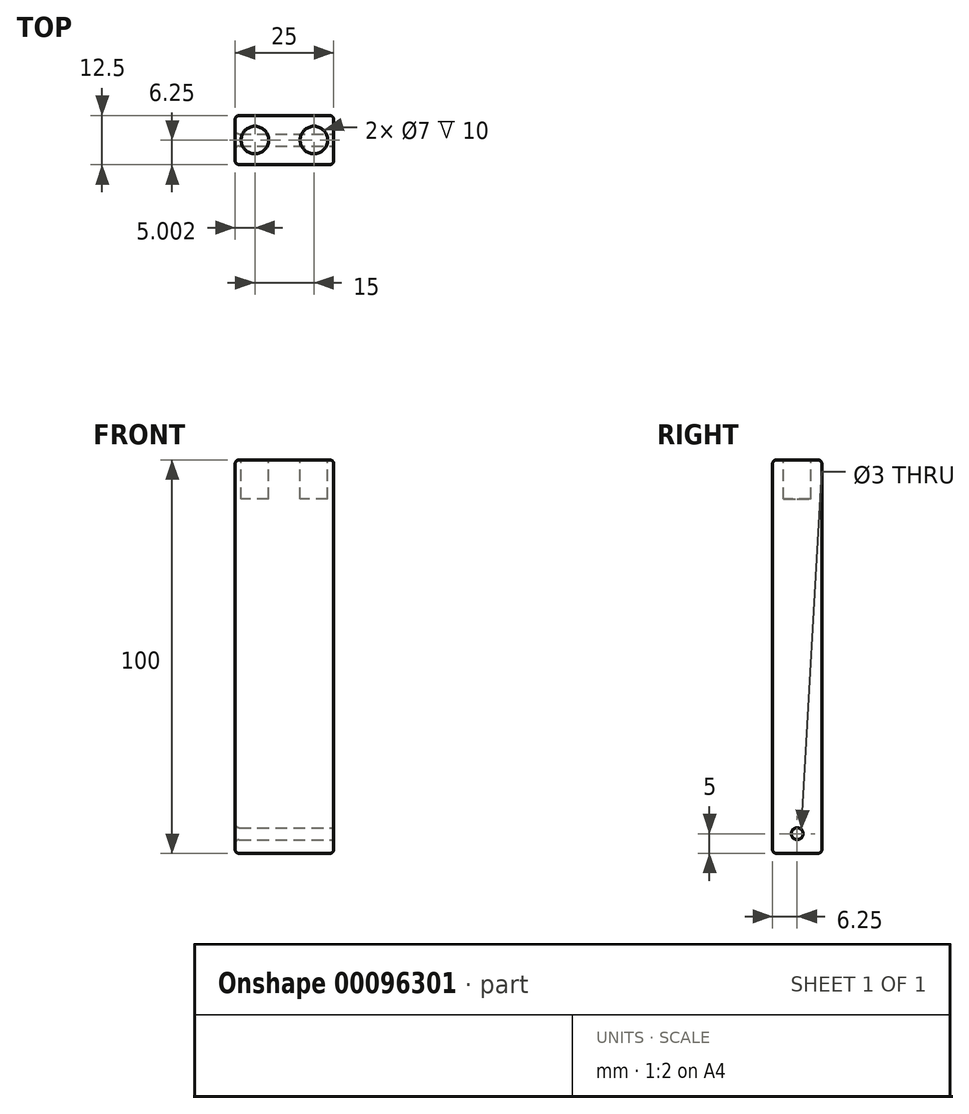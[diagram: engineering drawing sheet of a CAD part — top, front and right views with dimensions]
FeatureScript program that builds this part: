
annotation { "Feature Type Name" : "Feature", "Feature Type Description" : "" }
export const myFeature = defineFeature(function(context is Context, id is Id, definition is map)
    precondition{}
    {
        {
            var Q0;
            Q0=qCreatedBy(makeId("Front.planeOp"),FACE);
            var sketch = newSketch(context, id + "F0", { "sketchPlane" : qUnion([Q0])});
            skLineSegment(sketch, "E0.bottom", {"start": v(-26.19, 55.24) * mm, "end": v(-1.19, 55.24) * mm});
            skLineSegment(sketch, "E0.top", {"start": v(-26.19, -44.76) * mm, "end": v(-1.19, -44.76) * mm});
            skLineSegment(sketch, "E0.left", {"start": v(-26.19, 55.24) * mm, "end": v(-26.19, -44.76) * mm});
            skLineSegment(sketch, "E0.right", {"start": v(-1.19, 55.24) * mm, "end": v(-1.19, -44.76) * mm});
            skSolve(sketch);
        }
        {
            var Q0;
            Q0 = qSketchRegion(id + "F0", true);
            extrude(context, id + "F1", {"entities" : qUnion([Q0]), "depth" : 12.5 * mm});
        }
        {
            var Q0;
            Q0=qCreatedBy(makeId("Right.planeOp"),FACE);
            var sketch = newSketch(context, id + "F2", { "sketchPlane" : qUnion([Q0])});
            skCircle(sketch, "E1", {"center": v(-6.25, -39.76) * mm, "radius": 1.5 * mm});
            skSolve(sketch);
        }
        {
            var Q0;
            Q0 = qSketchRegion(id + "F2", true);
            extrude(context, id + "F3", {"entities" : qUnion([Q0]), "operationType" : NewBodyOperationType.REMOVE, "oppositeDirection" : true, "depth" : 27.2 * mm});
        }
        {
            var Q0;
            Q0=makeQuery(id+"F1.opExtrude","SWEPT_FACE",FACE,{"disambiguationData":[OSD([sQuery(id+"F0.wireOp",EDGE,"E0.bottom")])]});
            var sketch = newSketch(context, id + "F4", { "sketchPlane" : qUnion([Q0])});
            skCircle(sketch, "E2", {"center": v(-6.19, -6.25) * mm, "radius": 3.5 * mm});
            skCircle(sketch, "E3", {"center": v(-21.19, -6.25) * mm, "radius": 3.5 * mm});
            skSolve(sketch);
        }
        {
            var Q0;
            Q0 = qSketchRegion(id + "F4", true);
            extrude(context, id + "F5", {"entities" : qUnion([Q0]), "operationType" : NewBodyOperationType.REMOVE, "oppositeDirection" : true, "depth" : 10 * mm});
        }
        {
            var Q0;
            Q0=makeQuery(id+"F1.opExtrude","SWEPT_EDGE",EDGE,{"disambiguationData":[OSD([sQuery(id+"F0.wireOp",EDGE,"E0.bottom"),sQuery(id+"F0.wireOp",EDGE,"E0.left")])]});
            var Q1;
            Q1=makeQuery(id+"F1.opExtrude","CAP_EDGE",EDGE,{"disambiguationData":[OSD([sQuery(id+"F0.wireOp",EDGE,"E0.bottom")])],"isStart":false});
            var Q2;
            Q2=makeQuery(id+"F1.opExtrude","SWEPT_EDGE",EDGE,{"disambiguationData":[OSD([sQuery(id+"F0.wireOp",EDGE,"E0.bottom"),sQuery(id+"F0.wireOp",EDGE,"E0.right")])]});
            var Q3;
            Q3=makeQuery(id+"F1.opExtrude","CAP_EDGE",EDGE,{"disambiguationData":[OSD([sQuery(id+"F0.wireOp",EDGE,"E0.bottom")])],"isStart":true});
            var Q4;
            Q4=makeQuery(id+"F1.opExtrude","CAP_EDGE",EDGE,{"disambiguationData":[OSD([sQuery(id+"F0.wireOp",EDGE,"E0.left")])],"isStart":true});
            var Q5;
            Q5=makeQuery(id+"F1.opExtrude","CAP_EDGE",EDGE,{"disambiguationData":[OSD([sQuery(id+"F0.wireOp",EDGE,"E0.right")])],"isStart":true});
            var Q6;
            Q6=makeQuery(id+"F1.opExtrude","CAP_EDGE",EDGE,{"disambiguationData":[OSD([sQuery(id+"F0.wireOp",EDGE,"E0.top")])],"isStart":true});
            var Q7;
            Q7=makeQuery(id+"F1.opExtrude","CAP_EDGE",EDGE,{"disambiguationData":[OSD([sQuery(id+"F0.wireOp",EDGE,"E0.left")])],"isStart":false});
            var Q8;
            Q8=makeQuery(id+"F1.opExtrude","SWEPT_EDGE",EDGE,{"disambiguationData":[OSD([sQuery(id+"F0.wireOp",EDGE,"E0.top"),sQuery(id+"F0.wireOp",EDGE,"E0.left")])]});
            var Q9;
            Q9=makeQuery(id+"F3.boolean.opBoolean","INTERSECT",EDGE,{"derivedFrom":[makeQuery(id+"F1.opExtrude","SWEPT_FACE",FACE,{"disambiguationData":[OSD([sQuery(id+"F0.wireOp",EDGE,"E0.left")])]}),makeQuery(id+"F3.opExtrude","SWEPT_FACE",FACE,{"disambiguationData":[OSD([sQuery(id+"F2.wireOp",EDGE,"E1")])]})]});
            var Q10;
            Q10=makeQuery(id+"F1.opExtrude","CAP_EDGE",EDGE,{"disambiguationData":[OSD([sQuery(id+"F0.wireOp",EDGE,"E0.right")])],"isStart":false});
            var Q11;
            Q11=makeQuery(id+"F1.opExtrude","SWEPT_EDGE",EDGE,{"disambiguationData":[OSD([sQuery(id+"F0.wireOp",EDGE,"E0.top"),sQuery(id+"F0.wireOp",EDGE,"E0.right")])]});
            var Q12;
            Q12=makeQuery(id+"F5.boolean.opBoolean","COPY",EDGE,{"derivedFrom":makeQuery(id+"F5.opExtrude","CAP_EDGE",EDGE,{"disambiguationData":[OSD([sQuery(id+"F4.wireOp",EDGE,"E3")])],"isStart":true})});
            var Q13;
            Q13=makeQuery(id+"F5.boolean.opBoolean","COPY",EDGE,{"derivedFrom":makeQuery(id+"F5.opExtrude","CAP_EDGE",EDGE,{"disambiguationData":[OSD([sQuery(id+"F4.wireOp",EDGE,"E2")])],"isStart":true})});
            var Q14;
            Q14=makeQuery(id+"F1.opExtrude","CAP_EDGE",EDGE,{"disambiguationData":[OSD([sQuery(id+"F0.wireOp",EDGE,"E0.top")])],"isStart":false});
            fillet(context, id + "F6", {"entities" : qUnion([Q0, Q1, Q2, Q3, Q4, Q5, Q6, Q7, Q8, Q9, Q10, Q11, Q12, Q13, Q14]), "radius" : 1 * mm, "tangentPropagation" : true, "allowEdgeOverflow" : false});
        }
    });
